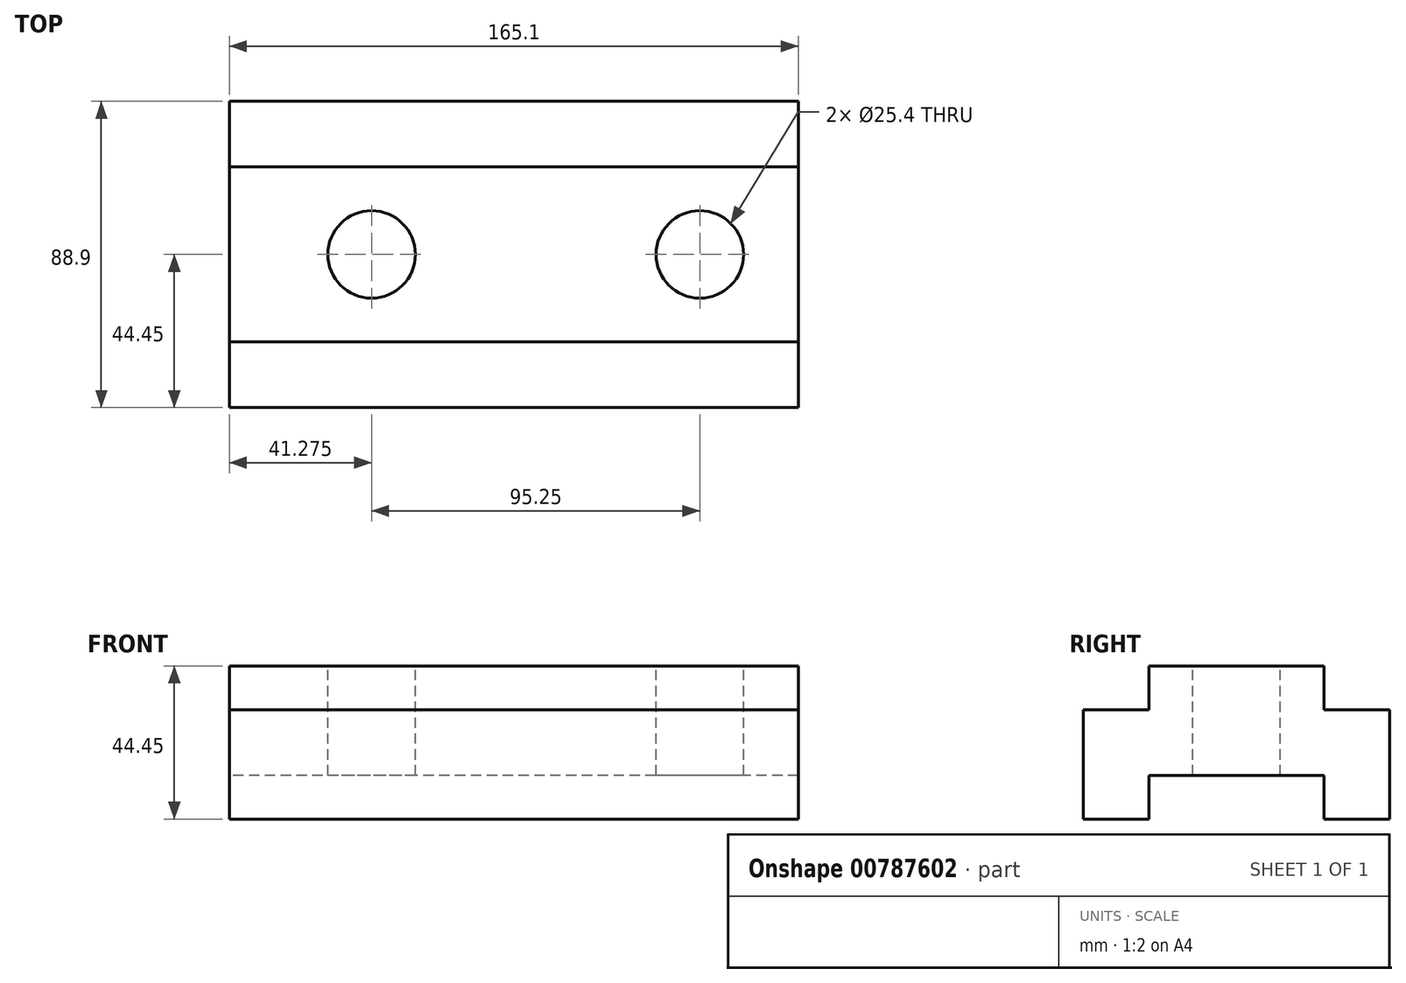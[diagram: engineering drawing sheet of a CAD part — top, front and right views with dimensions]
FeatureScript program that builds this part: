
annotation { "Feature Type Name" : "Feature", "Feature Type Description" : "" }
export const myFeature = defineFeature(function(context is Context, id is Id, definition is map)
    precondition{}
    {
        {
            var Q0;
            Q0=qCreatedBy(makeId("Right.planeOp"),FACE);
            var sketch = newSketch(context, id + "F0", { "sketchPlane" : qUnion([Q0])});
            skLineSegment(sketch, "E0", {"start": v(0, 0) * mm, "end": v(19.05, 0) * mm});
            skLineSegment(sketch, "E1", {"start": v(19.05, 0) * mm, "end": v(19.05, 12.7) * mm});
            skLineSegment(sketch, "E2", {"start": v(19.05, 12.7) * mm, "end": v(69.85, 12.7) * mm});
            skLineSegment(sketch, "E3", {"start": v(69.85, 12.7) * mm, "end": v(69.85, 0) * mm});
            skLineSegment(sketch, "E4", {"start": v(69.85, 0) * mm, "end": v(88.9, 0) * mm});
            skLineSegment(sketch, "E5", {"start": v(88.9, 0) * mm, "end": v(88.9, 31.75) * mm});
            skLineSegment(sketch, "E6", {"start": v(88.9, 31.75) * mm, "end": v(69.85, 31.75) * mm});
            skLineSegment(sketch, "E7", {"start": v(69.85, 31.75) * mm, "end": v(69.85, 44.45) * mm});
            skLineSegment(sketch, "E8", {"start": v(69.85, 44.45) * mm, "end": v(19.05, 44.45) * mm});
            skLineSegment(sketch, "E9", {"start": v(19.05, 44.45) * mm, "end": v(19.05, 31.75) * mm});
            skLineSegment(sketch, "E10", {"start": v(19.05, 31.75) * mm, "end": v(0, 31.75) * mm});
            skLineSegment(sketch, "E11", {"start": v(0, 31.75) * mm, "end": v(0, 0) * mm});
            skSolve(sketch);
        }
        {
            var Q0;
            Q0=makeQuery(id+"F0.imprint","IMPRINT",FACE,{"disambiguationData":[TD([[makeQuery(id+"F0.imprint","IMPRINT",EDGE,{"derivedFrom":sQuery(id+"F0.wireOp",EDGE,"E0")}),1.0]])]});
            extrude(context, id + "F1", {"entities" : qUnion([Q0]), "depth" : 165.1 * mm, "offsetDistance" : 25.4 * mm});
        }
        {
            var Q0;
            Q0=makeQuery(id+"F1.opExtrude","SWEPT_FACE",FACE,{"disambiguationData":[OSD([sQuery(id+"F0.wireOp",EDGE,"E8")])]});
            var sketch = newSketch(context, id + "F2", { "sketchPlane" : qUnion([Q0])});
            skLineSegment(sketch, "E12", {"start": v(0, 44.45) * mm, "end": v(41.28, 44.45) * mm, "construction": true});
            skLineSegment(sketch, "E13", {"start": v(41.28, 44.45) * mm, "end": v(136.53, 44.45) * mm, "construction": true});
            skCircle(sketch, "E14", {"center": v(41.28, 44.45) * mm, "radius": 12.7 * mm});
            skCircle(sketch, "E15", {"center": v(136.53, 44.45) * mm, "radius": 12.7 * mm});
            skSolve(sketch);
        }
        {
            var Q0;
            Q0=makeQuery(id+"F2.imprint","IMPRINT",FACE,{"disambiguationData":[TD([[makeQuery(id+"F2.imprint","IMPRINT",EDGE,{"derivedFrom":sQuery(id+"F2.wireOp",EDGE,"E14")}),1.0]])]});
            var Q1;
            Q1=makeQuery(id+"F2.imprint","IMPRINT",FACE,{"disambiguationData":[TD([[makeQuery(id+"F2.imprint","IMPRINT",EDGE,{"derivedFrom":sQuery(id+"F2.wireOp",EDGE,"E15")}),1.0]])]});
            extrude(context, id + "F3", {"entities" : qUnion([Q0, Q1]), "operationType" : NewBodyOperationType.REMOVE, "endBound" : BoundingType.THROUGH_ALL, "oppositeDirection" : true, "depth" : 25.4 * mm, "offsetDistance" : 25.4 * mm});
        }
    });
